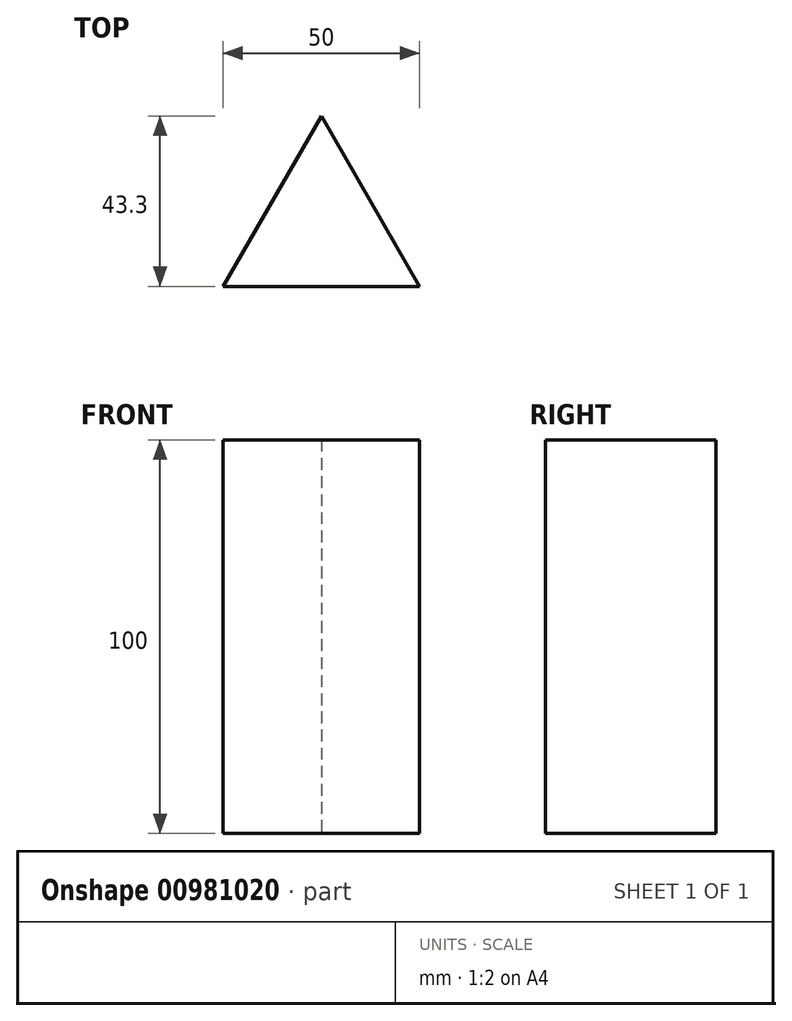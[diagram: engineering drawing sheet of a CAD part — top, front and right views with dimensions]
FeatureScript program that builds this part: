
annotation { "Feature Type Name" : "Feature", "Feature Type Description" : "" }
export const myFeature = defineFeature(function(context is Context, id is Id, definition is map)
    precondition{}
    {
        {
            var Q0;
            Q0=qCreatedBy(makeId("Top.planeOp"),FACE);
            var sketch = newSketch(context, id + "F0", { "sketchPlane" : qUnion([Q0])});
            skLineSegment(sketch, "E0", {"start": v(15.13, 30.58) * mm, "end": v(40.13, -12.72) * mm});
            skLineSegment(sketch, "E1", {"start": v(40.13, -12.72) * mm, "end": v(-9.87, -12.72) * mm});
            skLineSegment(sketch, "E2", {"start": v(-9.87, -12.72) * mm, "end": v(15.13, 30.58) * mm});
            skSolve(sketch);
        }
        {
            var Q0;
            Q0 = qSketchRegion(id + "F0", true);
            extrude(context, id + "F1", {"entities" : qUnion([Q0]), "depth" : 100 * mm, "offsetDistance" : 25 * mm});
        }
        {
            var Q0;
            Q0=makeQuery(id+"F1.opExtrude","CAP_FACE",FACE,{"disambiguationData":[OSD([sQuery(id+"F0.wireOp",EDGE,"E0"),sQuery(id+"F0.wireOp",EDGE,"E1"),sQuery(id+"F0.wireOp",EDGE,"E2")])],"isStart":true});
            var sketch = newSketch(context, id + "F2", { "sketchPlane" : qUnion([Q0])});
            skCircle(sketch, "E3", {"center": v(15.13, -1.71) * mm, "radius": 28.87 * mm});
            skPoint(sketch, "E3.first.point", {"position": v(40.13, 12.72) * mm});
            skPoint(sketch, "E3.second.point", {"position": v(-9.87, 12.72) * mm});
            skPoint(sketch, "E3.third.point", {"position": v(15.13, -30.58) * mm});
            skSolve(sketch);
        }
    });
